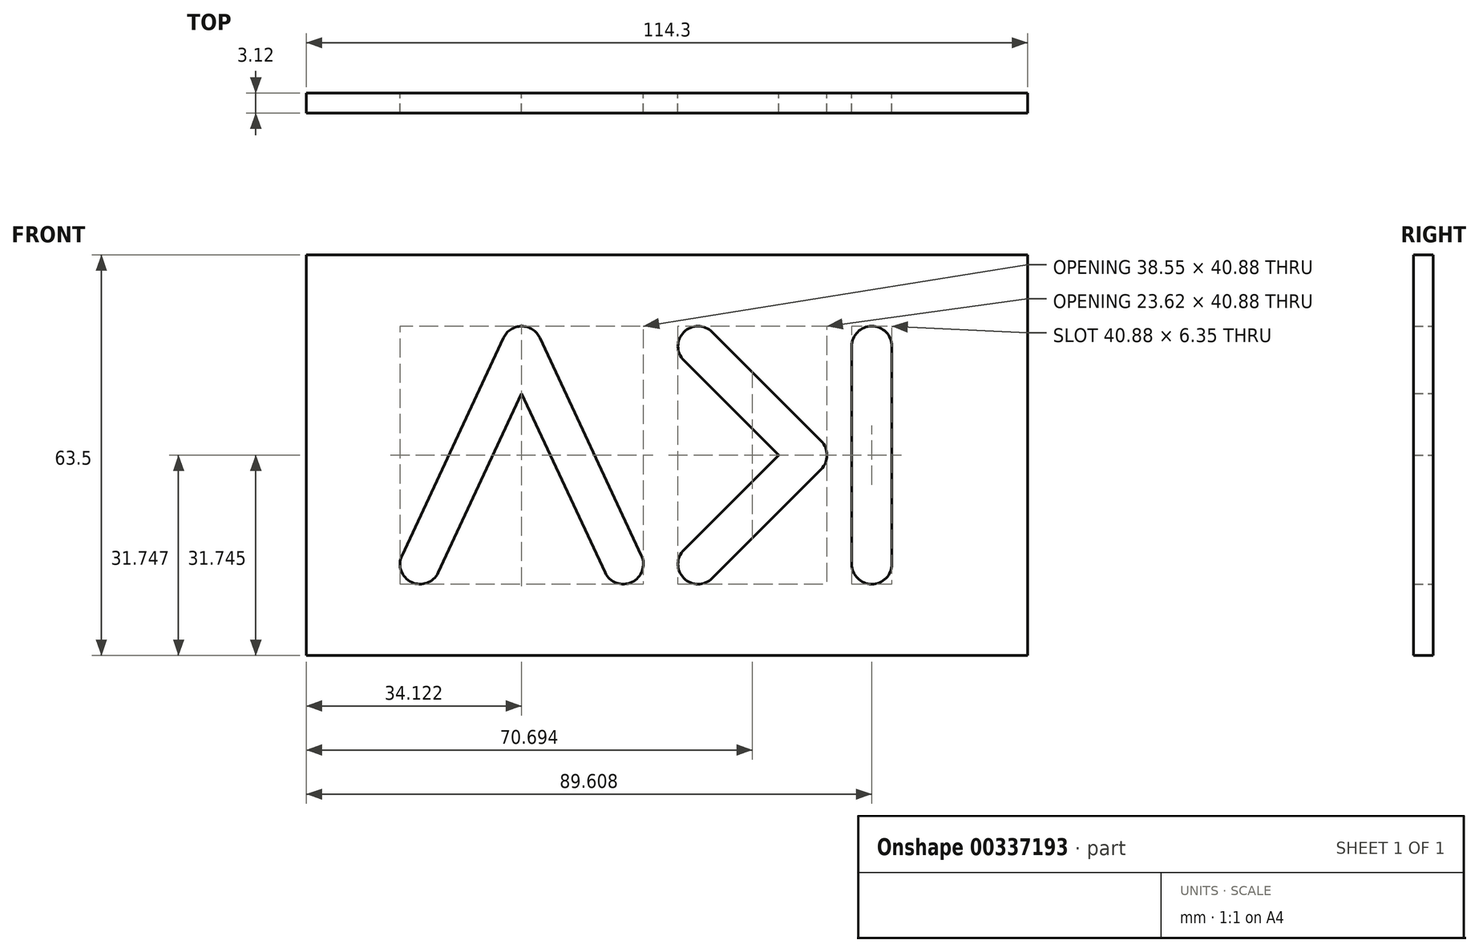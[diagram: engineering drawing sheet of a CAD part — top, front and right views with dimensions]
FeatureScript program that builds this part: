
annotation { "Feature Type Name" : "Feature", "Feature Type Description" : "" }
export const myFeature = defineFeature(function(context is Context, id is Id, definition is map)
    precondition{}
    {
        {
            var Q0;
            Q0=qCreatedBy(makeId("Front.planeOp"),FACE);
            var sketch = newSketch(context, id + "F0", { "sketchPlane" : qUnion([Q0])});
            skArc(sketch, "E0", {"start": v(-2.88, 1.34) * mm, "mid": v(-0.69, -3.1) * mm, "end": v(3.18, 0) * mm});
            skArc(sketch, "E1", {"start": v(18.98, 35.87) * mm, "mid": v(16.1, 37.7) * mm, "end": v(13.22, 35.87) * mm});
            skLineSegment(sketch, "E2", {"start": v(0, 0) * mm, "end": v(3.18, 0) * mm, "construction": true});
            skLineSegment(sketch, "E3", {"start": v(0, 0) * mm, "end": v(16.1, 34.53) * mm, "construction": true});
            skLineSegment(sketch, "E4", {"start": v(-2.88, 1.34) * mm, "end": v(13.22, 35.87) * mm});
            skLineSegment(sketch, "E5.MirrorCS", {"start": v(2.88, -1.34) * mm, "end": v(16.1, 27.02) * mm});
            skLineSegment(sketch, "E6", {"start": v(16.1, 34.53) * mm, "end": v(16.1, 0) * mm, "construction": true});
            skLineSegment(sketch, "E7.MirrorCS", {"start": v(32.2, 0) * mm, "end": v(29.03, 0) * mm, "construction": true});
            skArc(sketch, "E8.MirrorCS", {"start": v(35.08, 1.34) * mm, "mid": v(32.9, -3.1) * mm, "end": v(29.03, 0) * mm});
            skArc(sketch, "E9.MirrorCS", {"start": v(13.22, 35.87) * mm, "mid": v(16.1, 37.7) * mm, "end": v(18.98, 35.87) * mm});
            skLineSegment(sketch, "E10.MirrorCS", {"start": v(32.2, 0) * mm, "end": v(16.1, 34.53) * mm, "construction": true});
            skLineSegment(sketch, "E11.MirrorCS", {"start": v(35.08, 1.34) * mm, "end": v(18.98, 35.87) * mm});
            skLineSegment(sketch, "E12.MirrorCS", {"start": v(29.33, -1.34) * mm, "end": v(16.1, 27.02) * mm});
            skPoint(sketch, "E13.orphan", {"position": v(13.22, 33.19) * mm});
            skPoint(sketch, "E14.orphan", {"position": v(18.98, 33.19) * mm});
            skArc(sketch, "E15", {"start": v(41.8, 2.25) * mm, "mid": v(41.8, -2.25) * mm, "end": v(46.29, -2.25) * mm});
            skLineSegment(sketch, "E16", {"start": v(8.05, 17.27) * mm, "end": v(96.28, 17.27) * mm, "construction": true});
            skArc(sketch, "E17", {"start": v(63.55, 15.02) * mm, "mid": v(64.48, 17.27) * mm, "end": v(63.55, 19.51) * mm});
            skLineSegment(sketch, "E18", {"start": v(44.04, 0) * mm, "end": v(61.3, 17.27) * mm, "construction": true});
            skLineSegment(sketch, "E19", {"start": v(41.8, 2.25) * mm, "end": v(56.82, 17.27) * mm});
            skLineSegment(sketch, "E20.MirrorCS", {"start": v(46.29, -2.25) * mm, "end": v(63.55, 15.02) * mm});
            skLineSegment(sketch, "E21.MirrorCS", {"start": v(44.04, 34.53) * mm, "end": v(61.3, 17.27) * mm, "construction": true});
            skLineSegment(sketch, "E22.MirrorCS", {"start": v(46.29, 36.78) * mm, "end": v(63.55, 19.51) * mm});
            skArc(sketch, "E23.MirrorCS", {"start": v(63.55, 19.51) * mm, "mid": v(64.48, 17.27) * mm, "end": v(63.55, 15.02) * mm});
            skLineSegment(sketch, "E24.MirrorCS", {"start": v(41.8, 32.29) * mm, "end": v(56.82, 17.27) * mm});
            skArc(sketch, "E25.MirrorCS", {"start": v(41.8, 32.29) * mm, "mid": v(41.8, 36.78) * mm, "end": v(46.29, 36.78) * mm});
            skPoint(sketch, "E26.orphan", {"position": v(59.06, 15.02) * mm});
            skPoint(sketch, "E27.orphan", {"position": v(59.06, 19.51) * mm});
            skArc(sketch, "E28", {"start": v(68.41, 0) * mm, "mid": v(71.59, -3.18) * mm, "end": v(74.76, 0) * mm});
            skLineSegment(sketch, "E29", {"start": v(68.41, 0) * mm, "end": v(68.41, 17.27) * mm});
            skPoint(sketch, "E29.endSnap0", {"position": v(16.1, 17.27) * mm});
            skLineSegment(sketch, "E30", {"start": v(74.76, 0) * mm, "end": v(74.76, 17.27) * mm});
            skLineSegment(sketch, "E31.MirrorCS", {"start": v(68.41, 34.53) * mm, "end": v(68.41, 17.27) * mm});
            skArc(sketch, "E32.MirrorCS", {"start": v(68.41, 34.53) * mm, "mid": v(71.59, 37.7) * mm, "end": v(74.76, 34.53) * mm});
            skLineSegment(sketch, "E33.MirrorCS", {"start": v(74.76, 34.53) * mm, "end": v(74.76, 17.27) * mm});
            skLineSegment(sketch, "E34.bottom", {"start": v(-18.02, 49.02) * mm, "end": v(96.28, 49.02) * mm});
            skLineSegment(sketch, "E34.top", {"start": v(-18.02, -14.48) * mm, "end": v(96.28, -14.48) * mm});
            skLineSegment(sketch, "E34.left", {"start": v(-18.02, 49.02) * mm, "end": v(-18.02, -14.48) * mm});
            skLineSegment(sketch, "E34.right", {"start": v(96.28, 49.02) * mm, "end": v(96.28, -14.48) * mm});
            skSolve(sketch);
        }
        {
            var Q0;
            {var subQ4=sQuery(id+"F0.wireOp",EDGE,"E4");Q0=makeQuery(id+"F0.imprint","IMPRINT",FACE,{"disambiguationData":[TD([[makeQuery(id+"F0.imprint","IMPRINT",EDGE,{"derivedFrom":subQ4}),1.0]])]});}
            extrude(context, id + "F1", {"entities" : qUnion([Q0]), "depth" : 3.12 * mm});
        }
    });
